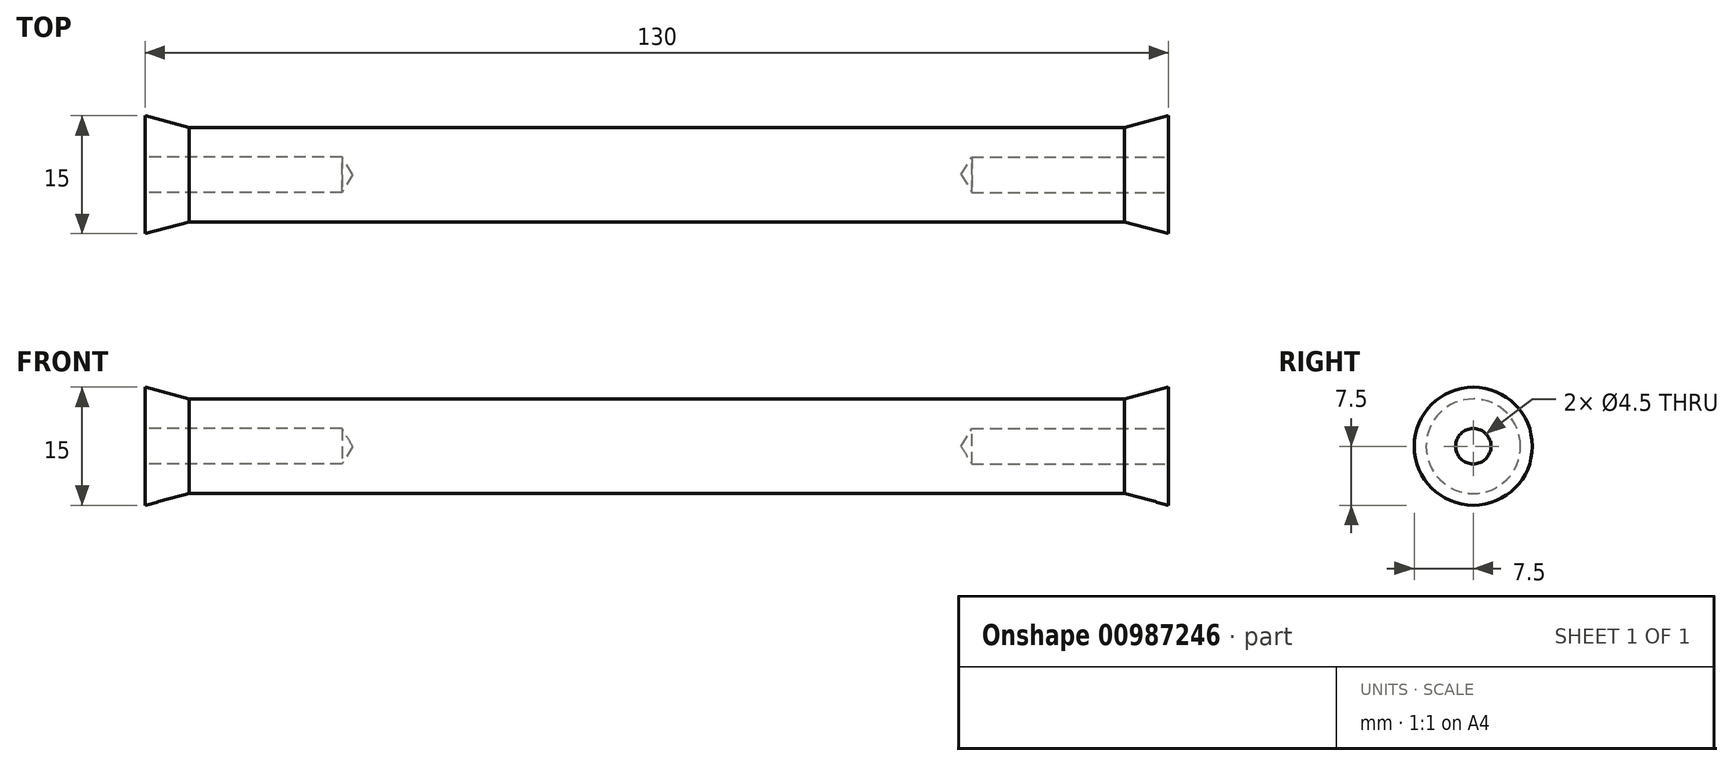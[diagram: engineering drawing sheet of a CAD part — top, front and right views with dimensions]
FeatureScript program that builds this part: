
annotation { "Feature Type Name" : "Feature", "Feature Type Description" : "" }
export const myFeature = defineFeature(function(context is Context, id is Id, definition is map)
    precondition{}
    {
        {
            var Q0;
            Q0=qCreatedBy(makeId("Front.planeOp"),FACE);
            var sketch = newSketch(context, id + "F0", { "sketchPlane" : qUnion([Q0])});
            skLineSegment(sketch, "E0", {"start": v(-65, 0) * mm, "end": v(-65, 7.5) * mm});
            skLineSegment(sketch, "E1", {"start": v(-65, 7.5) * mm, "end": v(-59.4, 6) * mm});
            skLineSegment(sketch, "E2", {"start": v(-59.4, 6) * mm, "end": v(59.4, 6) * mm});
            skLineSegment(sketch, "E3", {"start": v(59.4, 6) * mm, "end": v(65, 7.5) * mm});
            skLineSegment(sketch, "E4", {"start": v(65, 7.5) * mm, "end": v(65, 0) * mm});
            skLineSegment(sketch, "E5", {"start": v(65, 0) * mm, "end": v(-65, 0) * mm});
            skSolve(sketch);
        }
        {
            var Q0;
            Q0=makeQuery(id+"F0.imprint","IMPRINT",FACE,{"disambiguationData":[TD([[makeQuery(id+"F0.imprint","IMPRINT",EDGE,{"derivedFrom":sQuery(id+"F0.wireOp",EDGE,"E0")}),-1.0]])]});
            var Q1;
            Q1=sQuery(id+"F0.wireOp",EDGE,"E5");
            revolve(context, id + "F1", {"surfaceOperationType" : NewSurfaceOperationType.NEW, "entities" : qUnion([Q0]), "axis" : qUnion([Q1]), "revolveType" : RevolveType.FULL});
        }
        {
            var Q0;
            Q0=makeQuery(id+"F1.opRevolve","SWEPT_FACE",FACE,{"disambiguationData":[OSD([sQuery(id+"F0.wireOp",EDGE,"E0")])]});
            var sketch = newSketch(context, id + "F2", { "sketchPlane" : qUnion([Q0])});
            skPoint(sketch, "E6", {"position": v(0, 0) * mm});
            skSolve(sketch);
        }
        {
            var Q0;
            Q0=makeQuery(id+"F1.opRevolve","SWEPT_FACE",FACE,{"disambiguationData":[OSD([sQuery(id+"F0.wireOp",EDGE,"E4")])]});
            var sketch = newSketch(context, id + "F3", { "sketchPlane" : qUnion([Q0])});
            skPoint(sketch, "E7", {"position": v(0, 0) * mm});
            skSolve(sketch);
        }
        {
            var Q0;
            Q0=sQuery(id+"F2.wireOp",VERTEX,"E6");
            var Q1;
            Q1=sQuery(id+"F3.wireOp",VERTEX,"E7");
            var Q2;
            Q2=makeQuery(id+"F1.opRevolve","SWEPT_BODY",BODY,{"disambiguationData":[OSD([sQuery(id+"F0.wireOp",EDGE,"E0"),sQuery(id+"F0.wireOp",EDGE,"E1"),sQuery(id+"F0.wireOp",EDGE,"E2"),sQuery(id+"F0.wireOp",EDGE,"E3"),sQuery(id+"F0.wireOp",EDGE,"E4"),sQuery(id+"F0.wireOp",EDGE,"E5")])]});
            hole(context, id + "F4", {"style" : HoleStyle.SIMPLE, "endStyle" : HoleEndStyle.BLIND, "standardTappedOrClearance" : lookupTablePath({ "standard" : "ISO", "engagement" : "50%", "pitch" : "0.8 mm", "size" : "M5", "type" : "Tapped" }), "standardBlindInLast" : lookupTablePath({ "standard" : "ISO", "fit" : "Normal", "engagement" : "50%", "pitch" : "0.8 mm", "size" : "M5", "type" : "Clearance & tapped" }), "holeDiameter" : 4.5 * mm, "majorDiameter" : 5 * mm, "showTappedDepth" : true, "holeDepth" : 25 * mm, "isTappedThrough" : true, "tappedDepth" : 22.6 * mm, "tapClearance" : 3, "locations" : qUnion([Q0, Q1]), "scope" : qUnion([Q2])});
        }
    });
